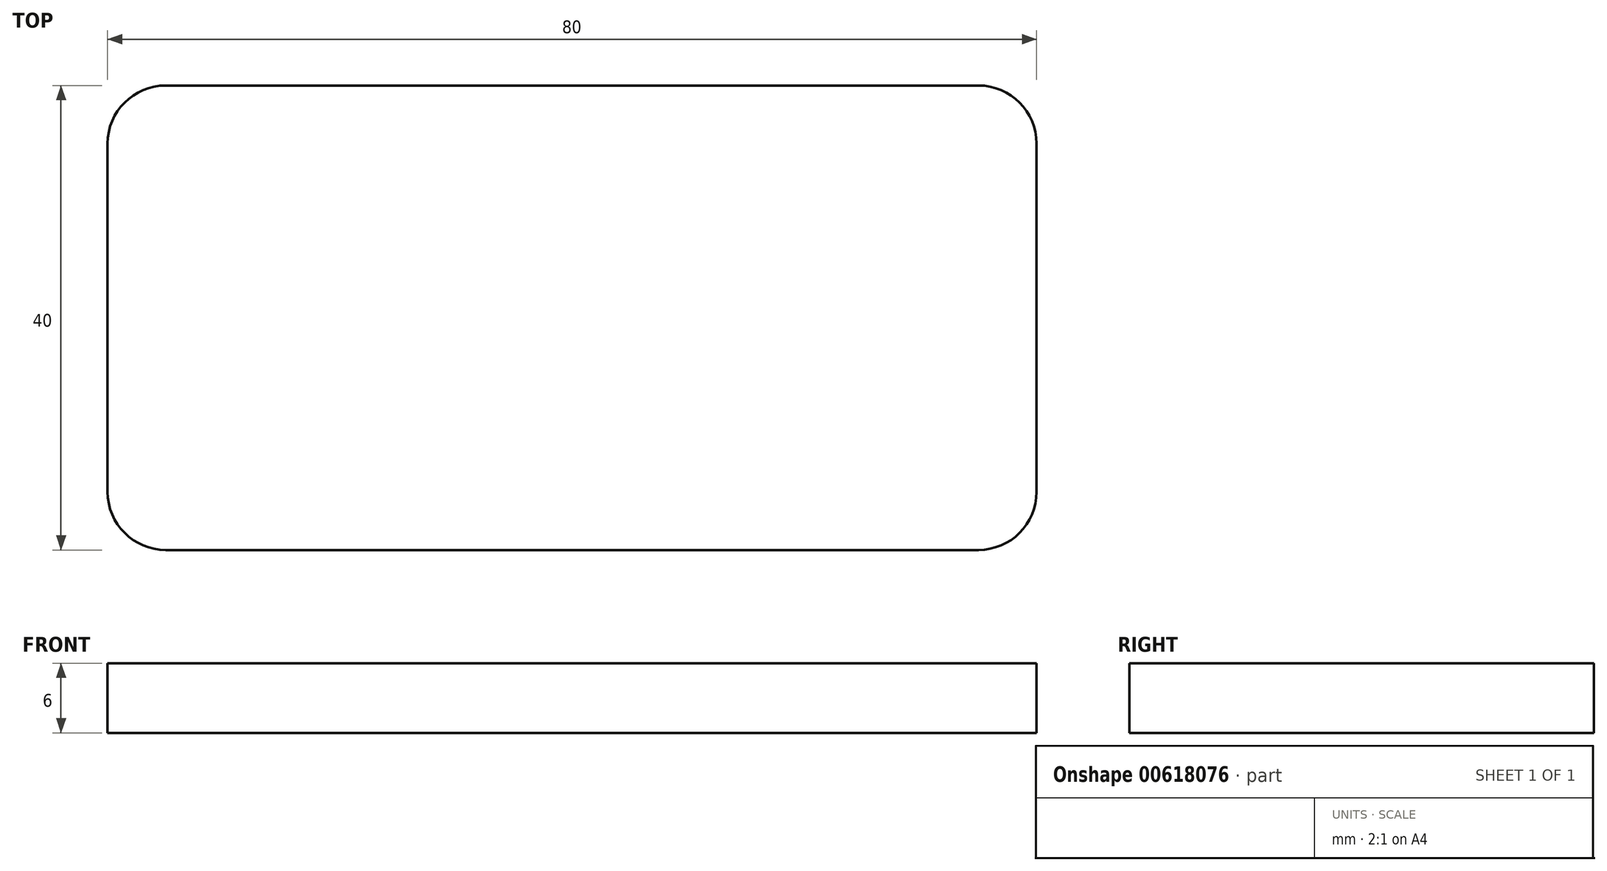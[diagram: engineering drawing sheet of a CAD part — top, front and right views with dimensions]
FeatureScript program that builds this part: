
annotation { "Feature Type Name" : "Feature", "Feature Type Description" : "" }
export const myFeature = defineFeature(function(context is Context, id is Id, definition is map)
    precondition{}
    {
        {
            var Q0;
            Q0=qCreatedBy(makeId("Top.planeOp"),FACE);
            var sketch = newSketch(context, id + "F0", { "sketchPlane" : qUnion([Q0])});
            skLineSegment(sketch, "E0.bottom", {"start": v(0, 0) * mm, "end": v(80, 0) * mm});
            skLineSegment(sketch, "E0.top", {"start": v(0, 40) * mm, "end": v(80, 40) * mm});
            skLineSegment(sketch, "E0.left", {"start": v(0, 0) * mm, "end": v(0, 40) * mm});
            skLineSegment(sketch, "E0.right", {"start": v(80, 0) * mm, "end": v(80, 40) * mm});
            skSolve(sketch);
        }
        {
            var Q0;
            Q0 = qSketchRegion(id + "F0", true);
            extrude(context, id + "F1", {"entities" : qUnion([Q0]), "depth" : 6 * mm, "offsetDistance" : 25 * mm});
        }
        {
            var Q0;
            Q0=makeQuery(id+"F1.opExtrude","SWEPT_EDGE",EDGE,{"disambiguationData":[OSD([sQuery(id+"F0.wireOp",EDGE,"E0.top"),sQuery(id+"F0.wireOp",EDGE,"E0.left")])]});
            fillet(context, id + "F2", {"entities" : qUnion([Q0]), "radius" : 5 * mm, "tangentPropagation" : true, "allowEdgeOverflow" : false});
        }
        {
            var Q0;
            Q0=makeQuery(id+"F1.opExtrude","SWEPT_EDGE",EDGE,{"disambiguationData":[OSD([sQuery(id+"F0.wireOp",EDGE,"E0.top"),sQuery(id+"F0.wireOp",EDGE,"E0.right")])]});
            fillet(context, id + "F3", {"entities" : qUnion([Q0]), "radius" : 5 * mm, "tangentPropagation" : true, "allowEdgeOverflow" : false});
        }
        {
            var Q0;
            Q0=makeQuery(id+"F1.opExtrude","SWEPT_EDGE",EDGE,{"disambiguationData":[OSD([sQuery(id+"F0.wireOp",EDGE,"E0.bottom"),sQuery(id+"F0.wireOp",EDGE,"E0.right")])]});
            fillet(context, id + "F4", {"entities" : qUnion([Q0]), "radius" : 5 * mm, "tangentPropagation" : true, "allowEdgeOverflow" : false});
        }
        {
            var Q0;
            Q0=makeQuery(id+"F1.opExtrude","SWEPT_EDGE",EDGE,{"disambiguationData":[OSD([sQuery(id+"F0.wireOp",EDGE,"E0.bottom"),sQuery(id+"F0.wireOp",EDGE,"E0.left")])]});
            fillet(context, id + "F5", {"entities" : qUnion([Q0]), "radius" : 5 * mm, "tangentPropagation" : true, "allowEdgeOverflow" : false});
        }
    });
